# Revit family: Aluco Skylight AIR (en)
name_source: partatom
category: Generic Models
units: mm (PartAtom-declared; Revit-internal decimal feet)

## family parameters
Always vertical = No
Can host rebar = No
Cut with Voids When Loaded = Yes
OmniClass Number = 23.60.70.14.11
OmniClass Title = Smoke Dampers
Part Type = Normal
Room Calculation Point = No
Round Connector Dimension = Use Diameter
Shared = No
Work Plane-Based = Yes

## types (2) — shared parameters
Breaking load resistance = UL 1500
Compressive load resistance = DL 2500
Description = Vents for daily ventilation dedicated to barrel vault skylights
Fire protection class = BRoof (t1)
IfcExportAs = "IfcWindowType"
Manufacturer = ALUCO SYSTEM SP. Z O.O
Model = Skylight AIR
Panel material = Aluco - polycarbonate
Product URL = https://aluco.com.pl
Profile material = Aluco - aluminum
Safety classification against drop from height = SB 1200
Type Comments = Ventilation vent
Type Image = ALUCO SKYLIGHT AIR.png
URL = https://aluco.com.pl
zero-valued in all types: Default Elevation

## per-type parameters (varying)
| type | Drive type | Power supply |
| with electric drive | electric drive | 230 V |
| with mechanical drive | mechanical drive | 0 V |
